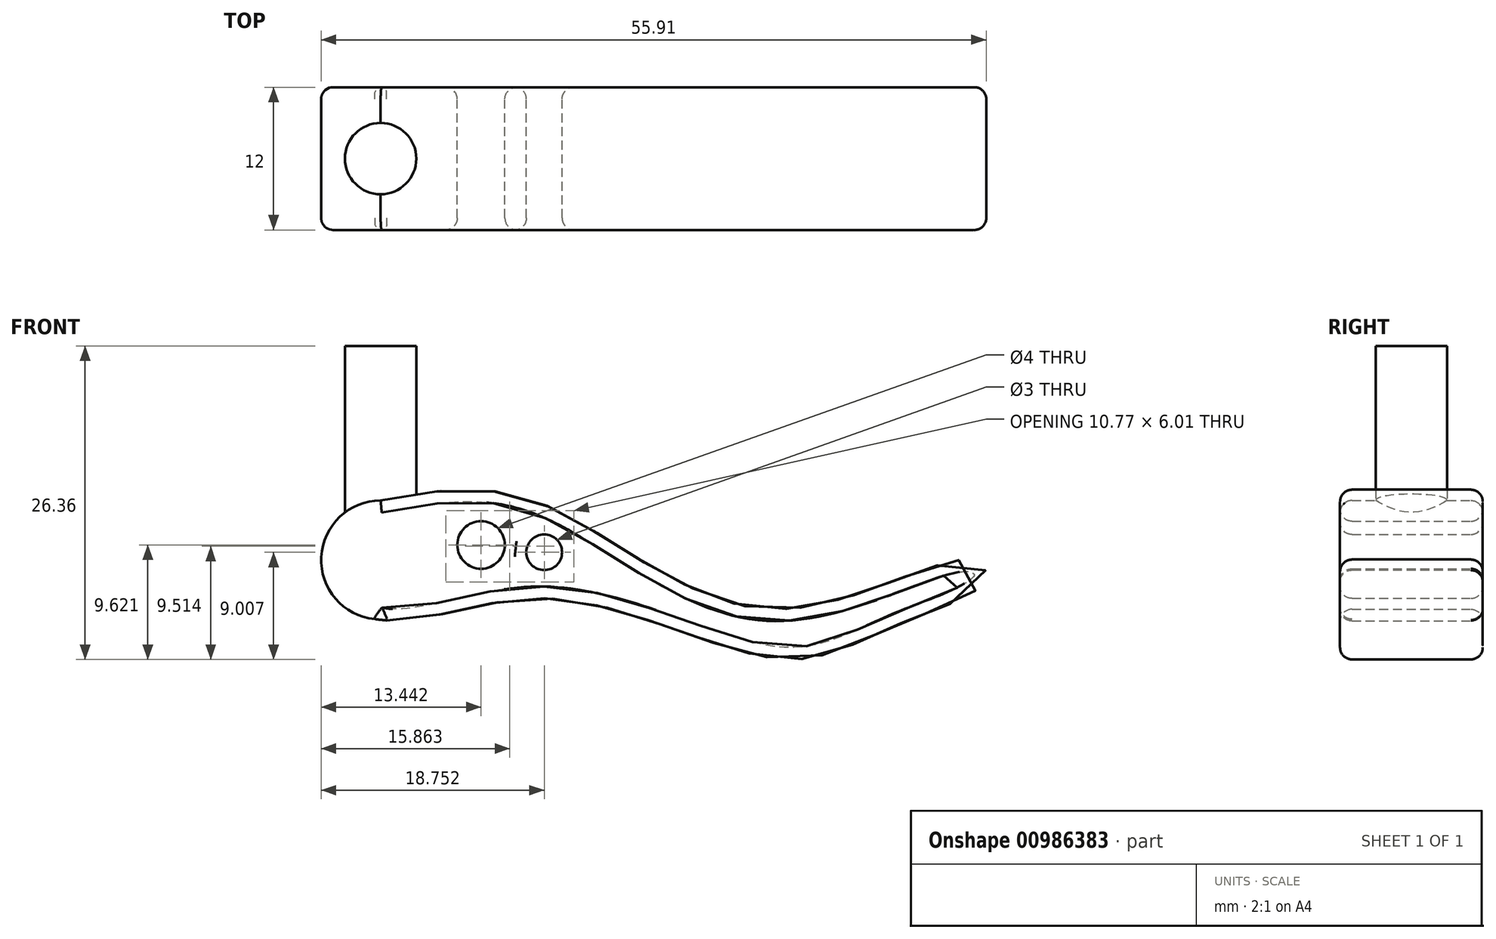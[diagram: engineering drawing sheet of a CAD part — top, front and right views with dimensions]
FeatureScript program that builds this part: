
annotation { "Feature Type Name" : "Feature", "Feature Type Description" : "" }
export const myFeature = defineFeature(function(context is Context, id is Id, definition is map)
    precondition{}
    {
        {
            var Q0;
            Q0=qCreatedBy(makeId("Front.planeOp"),FACE);
            var sketch = newSketch(context, id + "F0", { "sketchPlane" : qUnion([Q0])});
            skCircle(sketch, "E0", {"center": v(0, 0) * mm, "radius": 5 * mm});
            skLineSegment(sketch, "E1", {"start": v(0, 0) * mm, "end": v(49.6, -6.25) * mm, "construction": true});
            skFitSpline(sketch, "E2", {"points": [v(0, 5) * mm, v(13.27, 4.84) * mm, v(32.88, -4.14) * mm, v(49.65, 0) * mm, v(50.82, -1.68) * mm, v(43.4, -5.46) * mm, v(33.61, -8.33) * mm, v(14.18, -3.24) * mm, v(0, -5) * mm, v(-5, 0) * mm], "startDerivative": vector(109.9, 20.66) * mm, "endDerivative": vector(-46.95, 77.98) * mm});
            skCircle(sketch, "E3", {"center": v(8.44, 1.26) * mm, "radius": 2 * mm});
            skCircle(sketch, "E4", {"center": v(13.75, 0.65) * mm, "radius": 1.5 * mm});
            skSolve(sketch);
        }
        {
            var Q0;
            Q0 = qSketchRegion(id + "F0", true);
            extrude(context, id + "F1", {"entities" : qUnion([Q0]), "endBound" : BoundingType.SYMMETRIC, "depth" : 12 * mm, "offsetDistance" : 25 * mm});
        }
        {
            var Q0;
            Q0=makeQuery(id+"F1.opExtrude","CAP_FACE",FACE,{"disambiguationData":[OSD([sQuery(id+"F0.wireOp",EDGE,"E0"),sQuery(id+"F0.wireOp",EDGE,"E2"),sQuery(id+"F0.wireOp",EDGE,"E3"),sQuery(id+"F0.wireOp",EDGE,"E4"),sQuery(id+"F0.wireOp",EDGE,"VeKp7wx9-cD5q-6iZP-dHnu-nSsY8VwB2Au6")])],"isStart":false});
            var Q1;
            Q1=makeQuery(id+"F1.opExtrude","CAP_FACE",FACE,{"disambiguationData":[OSD([sQuery(id+"F0.wireOp",EDGE,"E0"),sQuery(id+"F0.wireOp",EDGE,"E2"),sQuery(id+"F0.wireOp",EDGE,"E3"),sQuery(id+"F0.wireOp",EDGE,"E4"),sQuery(id+"F0.wireOp",EDGE,"VeKp7wx9-cD5q-6iZP-dHnu-nSsY8VwB2Au6")])],"isStart":true});
            fillet(context, id + "F2", {"entities" : qUnion([Q0, Q1]), "tangentPropagation" : true, "radius" : 1 * mm, "defaultsChanged" : true, "vertexSettings" : [], "allowEdgeOverflow" : false});
        }
        {
            var Q0;
            {var subQ0=sQuery(id+"F0.wireOp",EDGE,"E2");var subQ1=sQuery(id+"F0.wireOp",EDGE,"E0");Q0=makeQuery(id+"F1.opExtrude","SWEPT_EDGE",EDGE,{"disambiguationData":[OSD([subQ1,subQ0]),TDD([makeQuery(id+"F0.imprint","INTERSECT",VERTEX,{"disambiguationData":[OD(0.0)],"derivedFrom":[subQ1,subQ0]})])]});}
            fillet(context, id + "F3", {"entities" : qUnion([Q0]), "tangentPropagation" : true, "radius" : 50 * mm, "defaultsChanged" : true, "vertexSettings" : [], "allowEdgeOverflow" : false});
        }
        {
            var Q0;
            Q0=qCreatedBy(makeId("Top.planeOp"),FACE);
            var sketch = newSketch(context, id + "F4", { "sketchPlane" : qUnion([Q0])});
            skCircle(sketch, "E5", {"center": v(0, 0) * mm, "radius": 3 * mm});
            skSolve(sketch);
        }
        {
            var Q0;
            Q0 = qSketchRegion(id + "F4", true);
            extrude(context, id + "F5", {"entities" : qUnion([Q0]), "operationType" : NewBodyOperationType.ADD, "depth" : 18 * mm, "offsetDistance" : 25 * mm});
        }
    });
